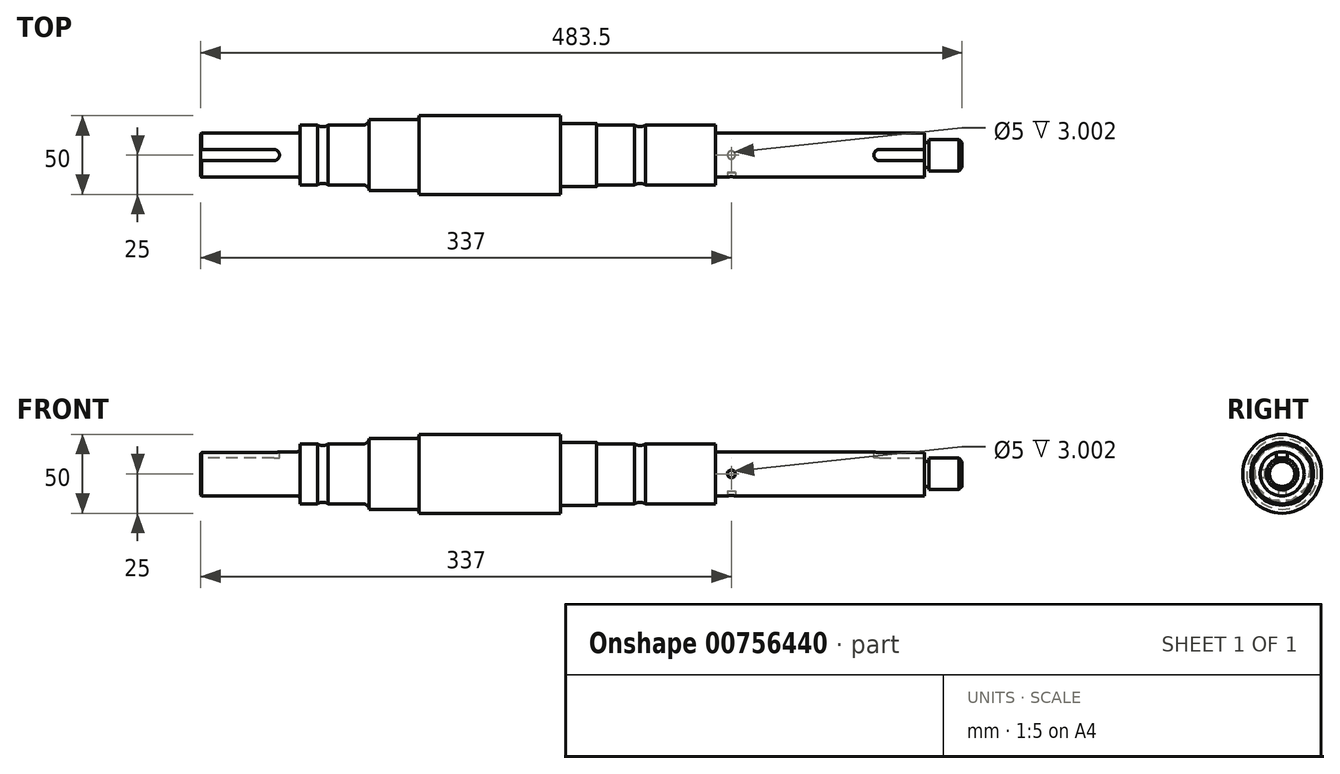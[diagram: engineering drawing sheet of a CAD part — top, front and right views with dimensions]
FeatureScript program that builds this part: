
annotation { "Feature Type Name" : "Feature", "Feature Type Description" : "" }
export const myFeature = defineFeature(function(context is Context, id is Id, definition is map)
    precondition{}
    {
        {
            var Q0;
            Q0=qCreatedBy(makeId("Front.planeOp"),FACE);
            var sketch = newSketch(context, id + "F0", { "sketchPlane" : qUnion([Q0])});
            skLineSegment(sketch, "E0", {"start": v(0, 14) * mm, "end": v(0, 0) * mm});
            skLineSegment(sketch, "E1", {"start": v(-23.92, 0) * mm, "end": v(518.13, 0) * mm, "construction": true});
            skLineSegment(sketch, "E2", {"start": v(0, 14) * mm, "end": v(63, 14) * mm});
            skLineSegment(sketch, "E3", {"start": v(63, 14) * mm, "end": v(63, 19) * mm});
            skLineSegment(sketch, "E4", {"start": v(63, 19) * mm, "end": v(74.1, 19) * mm});
            skArc(sketch, "E5", {"start": v(74.1, 19) * mm, "mid": v(77.5, 18) * mm, "end": v(80.9, 19) * mm});
            skLineSegment(sketch, "E6", {"start": v(80.9, 19) * mm, "end": v(107, 19) * mm});
            skLineSegment(sketch, "E7", {"start": v(107, 19) * mm, "end": v(107, 22.5) * mm});
            skLineSegment(sketch, "E8", {"start": v(107, 22.5) * mm, "end": v(138.5, 22.5) * mm});
            skLineSegment(sketch, "E9", {"start": v(138.5, 22.5) * mm, "end": v(138.5, 25) * mm});
            skLineSegment(sketch, "E10", {"start": v(138.5, 25) * mm, "end": v(228.5, 25) * mm});
            skLineSegment(sketch, "E11", {"start": v(228.5, 25) * mm, "end": v(228.5, 20) * mm});
            skLineSegment(sketch, "E12", {"start": v(228.5, 20) * mm, "end": v(251.5, 20) * mm});
            skLineSegment(sketch, "E13", {"start": v(251.5, 20) * mm, "end": v(251.5, 19) * mm});
            skLineSegment(sketch, "E14", {"start": v(251.5, 19) * mm, "end": v(275.6, 19) * mm});
            skArc(sketch, "E15", {"start": v(275.6, 19) * mm, "mid": v(279, 18) * mm, "end": v(282.4, 19) * mm});
            skLineSegment(sketch, "E16", {"start": v(282.4, 19) * mm, "end": v(327, 19) * mm});
            skLineSegment(sketch, "E17", {"start": v(327, 19) * mm, "end": v(327, 14) * mm});
            skLineSegment(sketch, "E18", {"start": v(327, 14) * mm, "end": v(459.5, 14) * mm});
            skLineSegment(sketch, "E19", {"start": v(459.5, 14) * mm, "end": v(459.5, 8) * mm});
            skLineSegment(sketch, "E20", {"start": v(459.5, 8) * mm, "end": v(462.5, 8) * mm});
            skLineSegment(sketch, "E21", {"start": v(462.5, 8) * mm, "end": v(462.5, 10) * mm});
            skLineSegment(sketch, "E22", {"start": v(462.5, 10) * mm, "end": v(483.5, 10) * mm});
            skLineSegment(sketch, "E23", {"start": v(483.5, 10) * mm, "end": v(483.5, 0) * mm});
            skLineSegment(sketch, "E24", {"start": v(77.5, 18) * mm, "end": v(92.45, 18) * mm, "construction": true});
            skLineSegment(sketch, "E25", {"start": v(279, 18) * mm, "end": v(283.85, 18) * mm, "construction": true});
            skLineSegment(sketch, "E26", {"start": v(0, 0) * mm, "end": v(483.5, 0) * mm});
            skSolve(sketch);
        }
        {
            var Q0;
            Q0 = qSketchRegion(id + "F0", true);
            var Q1;
            Q1=sQuery(id+"F0.wireOp",EDGE,"E1");
            revolve(context, id + "F1", {"surfaceOperationType" : NewSurfaceOperationType.NEW, "entities" : qUnion([Q0]), "axis" : qUnion([Q1]), "revolveType" : RevolveType.FULL});
        }
        {
            var Q0;
            Q0=makeQuery(id+"F1.opRevolve","SWEPT_EDGE",EDGE,{"disambiguationData":[OSD([sQuery(id+"F0.wireOp",EDGE,"E0"),sQuery(id+"F0.wireOp",EDGE,"E2")])]});
            chamfer(context, id + "F2", {"entities" : qUnion([Q0]), "width" : 0.5 * mm, "tangentPropagation" : true});
        }
        {
            var Q0;
            Q0=makeQuery(id+"F1.opRevolve","SWEPT_EDGE",EDGE,{"disambiguationData":[OSD([sQuery(id+"F0.wireOp",EDGE,"E2"),sQuery(id+"F0.wireOp",EDGE,"E3")])]});
            fillet(context, id + "F3", {"entities" : qUnion([Q0]), "radius" : 2 * mm, "tangentPropagation" : true, "allowEdgeOverflow" : false});
        }
        {
            var Q0;
            Q0=makeQuery(id+"F1.opRevolve","SWEPT_EDGE",EDGE,{"disambiguationData":[OSD([sQuery(id+"F0.wireOp",EDGE,"E6"),sQuery(id+"F0.wireOp",EDGE,"E7")])]});
            fillet(context, id + "F4", {"entities" : qUnion([Q0]), "radius" : 4 * mm, "tangentPropagation" : true, "allowEdgeOverflow" : false});
        }
        {
            var Q0;
            Q0=makeQuery(id+"F1.opRevolve","SWEPT_EDGE",EDGE,{"disambiguationData":[OSD([sQuery(id+"F0.wireOp",EDGE,"E8"),sQuery(id+"F0.wireOp",EDGE,"E9")])]});
            fillet(context, id + "F5", {"entities" : qUnion([Q0]), "radius" : 1.5 * mm, "tangentPropagation" : true, "allowEdgeOverflow" : false});
        }
        {
            var Q0;
            Q0=makeQuery(id+"F1.opRevolve","SWEPT_EDGE",EDGE,{"disambiguationData":[OSD([sQuery(id+"F0.wireOp",EDGE,"E11"),sQuery(id+"F0.wireOp",EDGE,"E12")])]});
            fillet(context, id + "F6", {"entities" : qUnion([Q0]), "radius" : 1.5 * mm, "tangentPropagation" : true, "allowEdgeOverflow" : false});
        }
        {
            var Q0;
            Q0=makeQuery(id+"F1.opRevolve","SWEPT_EDGE",EDGE,{"disambiguationData":[OSD([sQuery(id+"F0.wireOp",EDGE,"E13"),sQuery(id+"F0.wireOp",EDGE,"E14")])]});
            var Q1;
            Q1=makeQuery(id+"F1.opRevolve","SWEPT_EDGE",EDGE,{"disambiguationData":[OSD([sQuery(id+"F0.wireOp",EDGE,"E17"),sQuery(id+"F0.wireOp",EDGE,"E18")])]});
            fillet(context, id + "F7", {"entities" : qUnion([Q0, Q1]), "radius" : 1.5 * mm, "tangentPropagation" : true, "allowEdgeOverflow" : false});
        }
        {
            var Q0;
            Q0=makeQuery(id+"F1.opRevolve","SWEPT_EDGE",EDGE,{"disambiguationData":[OSD([sQuery(id+"F0.wireOp",EDGE,"E22"),sQuery(id+"F0.wireOp",EDGE,"E23")])]});
            chamfer(context, id + "F8", {"entities" : qUnion([Q0]), "width" : 2 * mm, "tangentPropagation" : true});
        }
        {
            var Q0;
            Q0=qCreatedBy(makeId("Top.planeOp"),FACE);
            cPlane(context, id + "F9", {"entities" : qUnion([Q0]), "cplaneType" : CPlaneType.OFFSET, "offset" : 14 * mm, "width" : 150 * mm, "height" : 150 * mm});
        }
        {
            var Q0;
            Q0=qCreatedBy(id+"F9.planeOp",FACE);
            var sketch = newSketch(context, id + "F10", { "sketchPlane" : qUnion([Q0])});
            skLineSegment(sketch, "E27", {"start": v(0, 3.5) * mm, "end": v(0, -3.5) * mm});
            skLineSegment(sketch, "E28", {"start": v(0, -3.5) * mm, "end": v(46.5, -3.5) * mm});
            skArc(sketch, "E29", {"start": v(46.5, -3.5) * mm, "mid": v(50, 0) * mm, "end": v(46.5, 3.5) * mm});
            skLineSegment(sketch, "E30", {"start": v(46.5, 3.5) * mm, "end": v(0, 3.5) * mm});
            skSolve(sketch);
        }
        {
            var Q0;
            Q0 = qSketchRegion(id + "F10", true);
            extrude(context, id + "F11", {"entities" : qUnion([Q0]), "operationType" : NewBodyOperationType.REMOVE, "oppositeDirection" : true, "depth" : 4 * mm, "offsetDistance" : 25 * mm});
        }
        {
            var Q0;
            Q0=qCreatedBy(id+"F9.planeOp",FACE);
            var sketch = newSketch(context, id + "F12", { "sketchPlane" : qUnion([Q0])});
            skLineSegment(sketch, "E31.0", {"start": v(459.5, -14) * mm, "end": v(459.5, 14) * mm});
            skLineSegment(sketch, "E32", {"start": v(489.37, 0) * mm, "end": v(425.52, 0) * mm, "construction": true});
            skPoint(sketch, "E32.startSnap0", {"position": v(459.5, 0) * mm});
            skLineSegment(sketch, "E33", {"start": v(459.5, 3.5) * mm, "end": v(431, 3.5) * mm});
            skLineSegment(sketch, "E34", {"start": v(431, -3.5) * mm, "end": v(459.5, -3.5) * mm});
            skArc(sketch, "E35", {"start": v(431, 3.5) * mm, "mid": v(427.5, 0) * mm, "end": v(431, -3.5) * mm});
            skSolve(sketch);
        }
        {
            var Q0;
            Q0 = qSketchRegion(id + "F12", true);
            extrude(context, id + "F13", {"entities" : qUnion([Q0]), "operationType" : NewBodyOperationType.REMOVE, "oppositeDirection" : true, "depth" : 4 * mm, "offsetDistance" : 25 * mm});
        }
        {
            var Q0;
            Q0=qCreatedBy(makeId("Front.planeOp"),FACE);
            cPlane(context, id + "F14", {"entities" : qUnion([Q0]), "cplaneType" : CPlaneType.OFFSET, "offset" : 14 * mm, "width" : 150 * mm, "height" : 150 * mm});
        }
        {
            var Q0;
            Q0=qCreatedBy(id+"F14.planeOp",FACE);
            var sketch = newSketch(context, id + "F15", { "sketchPlane" : qUnion([Q0])});
            skLineSegment(sketch, "E36.0", {"start": v(459.5, 13.56) * mm, "end": v(459.5, -14) * mm});
            skLineSegment(sketch, "E37", {"start": v(459.5, 0) * mm, "end": v(327, 0) * mm});
            skCircle(sketch, "E38", {"center": v(337, 0) * mm, "radius": 2.5 * mm});
            skLineSegment(sketch, "E39.0", {"start": v(327, -19) * mm, "end": v(327, 19) * mm});
            skSolve(sketch);
        }
        {
            var Q0;
            Q0 = qSketchRegion(id + "F15", true);
            extrude(context, id + "F16", {"entities" : qUnion([Q0]), "operationType" : NewBodyOperationType.REMOVE, "oppositeDirection" : true, "depth" : 3 * mm, "offsetDistance" : 25 * mm});
        }
        {
            var Q0;
            Q0=qCreatedBy(makeId("Top.planeOp"),FACE);
            cPlane(context, id + "F17", {"entities" : qUnion([Q0]), "cplaneType" : CPlaneType.OFFSET, "offset" : 14 * mm, "oppositeDirection" : true, "width" : 150 * mm, "height" : 150 * mm});
        }
        {
            var Q0;
            Q0=qCreatedBy(id+"F17.planeOp",FACE);
            var sketch = newSketch(context, id + "F18", { "sketchPlane" : qUnion([Q0])});
            skLineSegment(sketch, "E40.0", {"start": v(327, -19) * mm, "end": v(327, 19) * mm});
            skLineSegment(sketch, "E41", {"start": v(327, 0) * mm, "end": v(393.32, 0) * mm});
            skCircle(sketch, "E42", {"center": v(337, 0) * mm, "radius": 2.5 * mm});
            skSolve(sketch);
        }
        {
            var Q0;
            Q0 = qSketchRegion(id + "F18", true);
            extrude(context, id + "F19", {"entities" : qUnion([Q0]), "operationType" : NewBodyOperationType.REMOVE, "depth" : 3 * mm, "offsetDistance" : 25 * mm});
        }
    });
